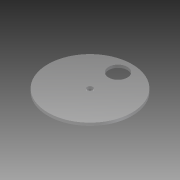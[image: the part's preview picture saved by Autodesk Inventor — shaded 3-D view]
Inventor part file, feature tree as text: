
AUTODESK INVENTOR PART (.ipt)
format: ipt  version: 2012 (Build 160160000, 160)  size: 76,800 bytes
history: native  units: mm
features: extrude x1, sketch x1
ambient origin geometry x8: Origin, YZ Plane, XZ Plane, XY Plane, X Axis, Y Axis, Z Axis, Center Point
feature tree (2):
  extrude  "Extrusion2"  Depth=5.9mm
  sketch  "Sketch1"  dims[d0=90.0mm d1=5.9mm d4=20.0mm d6=30.0mm d7=3.0mm d8=0.0mm]
